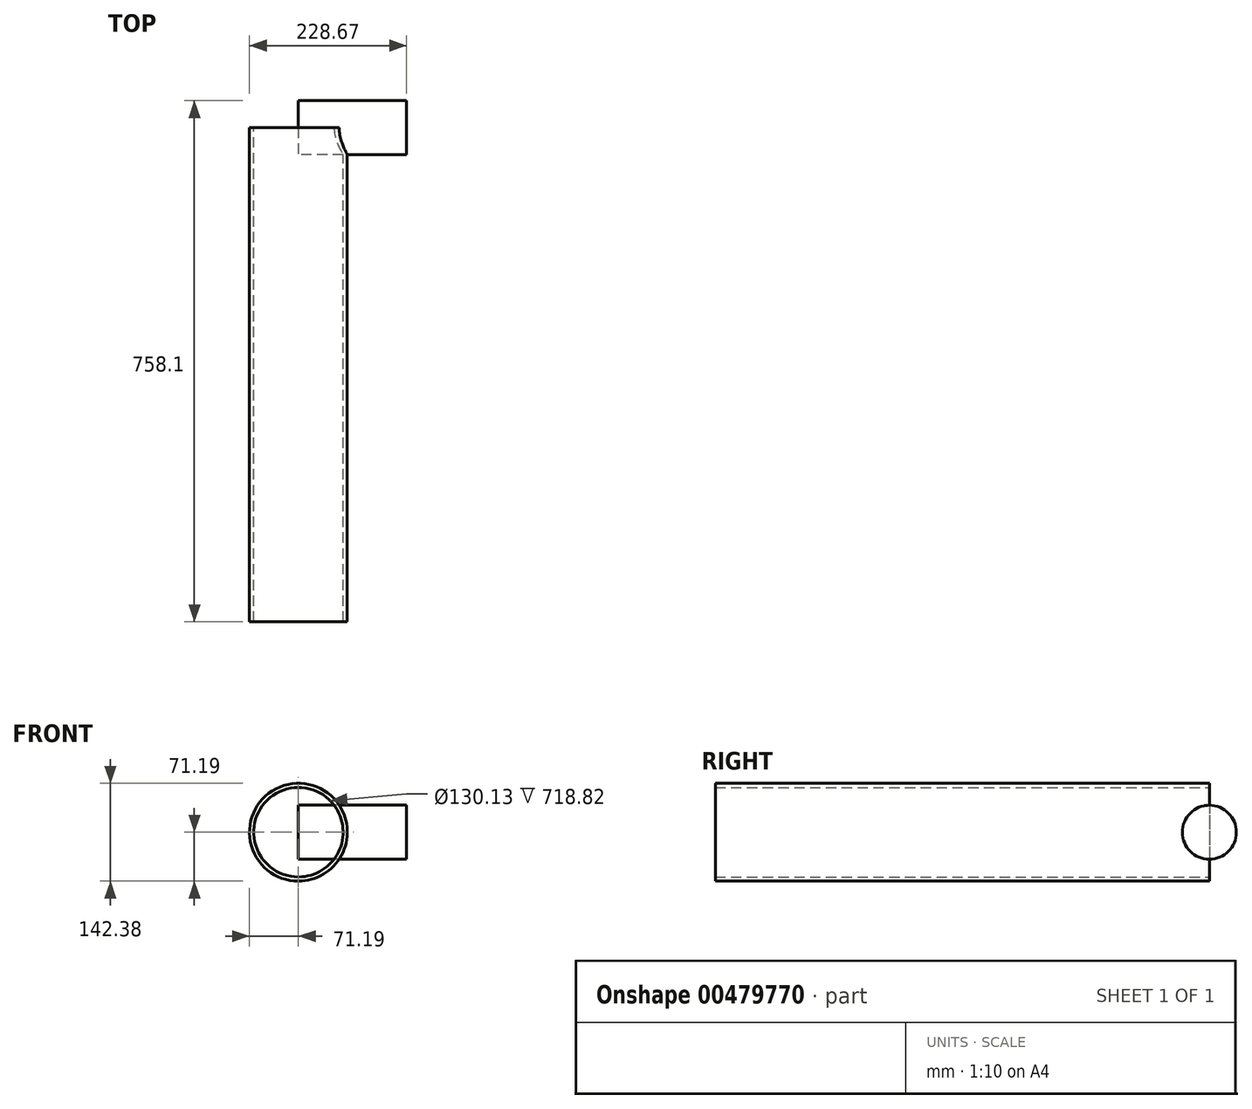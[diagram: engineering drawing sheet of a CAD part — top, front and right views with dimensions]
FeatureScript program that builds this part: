
annotation { "Feature Type Name" : "Feature", "Feature Type Description" : "" }
export const myFeature = defineFeature(function(context is Context, id is Id, definition is map)
    precondition{}
    {
        {
            var Q0;
            Q0=qCreatedBy(makeId("Front.planeOp"),FACE);
            var sketch = newSketch(context, id + "F0", { "sketchPlane" : qUnion([Q0])});
            skCircle(sketch, "E0", {"center": v(0, 0) * mm, "radius": 71.19 * mm});
            skCircle(sketch, "E1", {"center": v(0, 0) * mm, "radius": 65.06 * mm});
            skSolve(sketch);
        }
        {
            var Q0;
            Q0 = qSketchRegion(id + "F0", true);
            extrude(context, id + "F1", {"entities" : qUnion([Q0]), "depth" : 718.82 * mm});
        }
        {
            var Q0;
            Q0=qCreatedBy(makeId("Right.planeOp"),FACE);
            var sketch = newSketch(context, id + "F2", { "sketchPlane" : qUnion([Q0])});
            skCircle(sketch, "E2", {"center": v(0, 0) * mm, "radius": 39.28 * mm});
            skCircle(sketch, "E3", {"center": v(0, 0) * mm, "radius": 26.18 * mm});
            skSolve(sketch);
        }
        {
            var Q0;
            Q0=makeQuery(id+"F2.imprint","IMPRINT",FACE,{"disambiguationData":[TD([[makeQuery(id+"F2.imprint","IMPRINT",EDGE,{"derivedFrom":sQuery(id+"F2.wireOp",EDGE,"E2")}),1.0]])]});
            var Q1;
            Q1=makeQuery(id+"F2.imprint","IMPRINT",FACE,{"disambiguationData":[TD([[makeQuery(id+"F2.imprint","IMPRINT",EDGE,{"derivedFrom":sQuery(id+"F2.wireOp",EDGE,"E3")}),1.0]])]});
            extrude(context, id + "F3", {"entities" : qUnion([Q0, Q1]), "operationType" : NewBodyOperationType.ADD, "depth" : 157.48 * mm});
        }
    });
